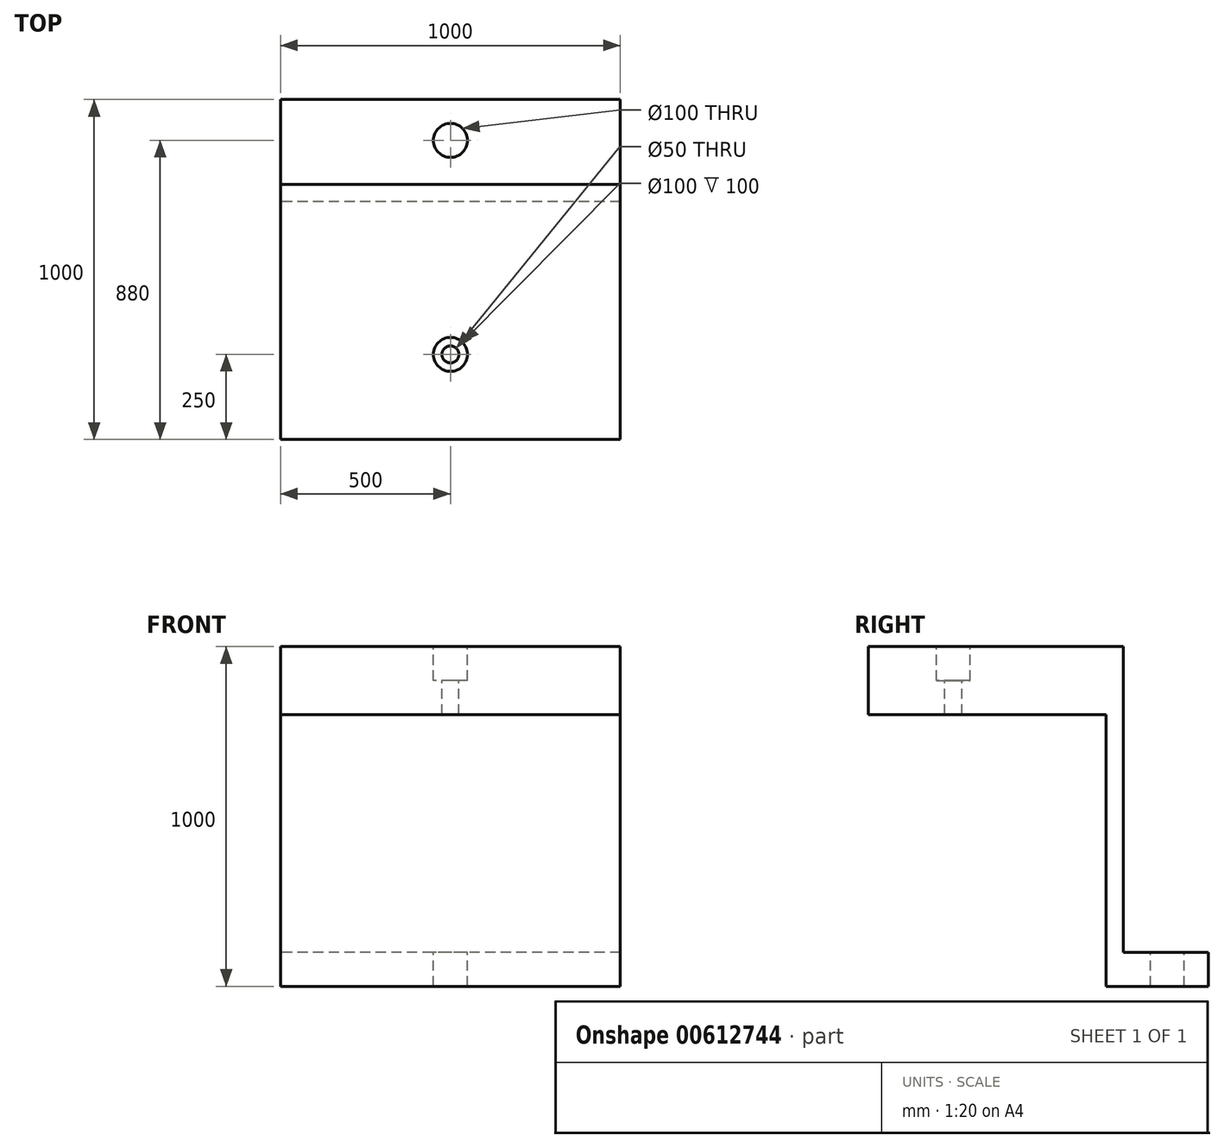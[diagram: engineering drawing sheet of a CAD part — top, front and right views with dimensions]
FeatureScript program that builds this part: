
annotation { "Feature Type Name" : "Feature", "Feature Type Description" : "" }
export const myFeature = defineFeature(function(context is Context, id is Id, definition is map)
    precondition{}
    {
        {
            var Q0;
            Q0=qCreatedBy(makeId("Right.planeOp"),FACE);
            var sketch = newSketch(context, id + "F0", { "sketchPlane" : qUnion([Q0])});
            skLineSegment(sketch, "E0", {"start": v(0, 0) * mm, "end": v(0, 100) * mm});
            skLineSegment(sketch, "E1", {"start": v(0, 100) * mm, "end": v(-250, 100) * mm});
            skLineSegment(sketch, "E2", {"start": v(-250, 100) * mm, "end": v(-250, 1000) * mm});
            skLineSegment(sketch, "E3", {"start": v(-250, 1000) * mm, "end": v(-1000, 1000) * mm});
            skLineSegment(sketch, "E4", {"start": v(-1000, 1000) * mm, "end": v(-1000, 800) * mm});
            skLineSegment(sketch, "E5", {"start": v(-1000, 800) * mm, "end": v(-300, 800) * mm});
            skLineSegment(sketch, "E6", {"start": v(-300, 800) * mm, "end": v(-300, 0) * mm});
            skLineSegment(sketch, "E7", {"start": v(0, 0) * mm, "end": v(-300, 0) * mm});
            skSolve(sketch);
        }
        {
            var Q0;
            Q0=makeQuery(id+"F0.imprint","IMPRINT",FACE,{"disambiguationData":[TD([[makeQuery(id+"F0.imprint","IMPRINT",EDGE,{"derivedFrom":sQuery(id+"F0.wireOp",EDGE,"E0")}),1.0]])]});
            extrude(context, id + "F1", {"entities" : qUnion([Q0]), "depth" : 1000 * mm, "offsetDistance" : 25 * mm});
        }
        {
            var Q0;
            Q0=makeQuery(id+"F1.opExtrude","SWEPT_FACE",FACE,{"disambiguationData":[OSD([sQuery(id+"F0.wireOp",EDGE,"E1")])]});
            var sketch = newSketch(context, id + "F2", { "sketchPlane" : qUnion([Q0])});
            skPoint(sketch, "E8", {"position": v(500, -120) * mm});
            skSolve(sketch);
        }
        {
            var Q0;
            Q0=sQuery(id+"F2.wireOp",VERTEX,"E8");
            var Q1;
            Q1=makeQuery(id+"F1.opExtrude","SWEPT_BODY",BODY,{"disambiguationData":[OSD([sQuery(id+"F0.wireOp",EDGE,"E0"),sQuery(id+"F0.wireOp",EDGE,"E1"),sQuery(id+"F0.wireOp",EDGE,"E2"),sQuery(id+"F0.wireOp",EDGE,"E3"),sQuery(id+"F0.wireOp",EDGE,"E4"),sQuery(id+"F0.wireOp",EDGE,"E5"),sQuery(id+"F0.wireOp",EDGE,"E6"),sQuery(id+"F0.wireOp",EDGE,"E7")])]});
            hole(context, id + "F3", {"style" : HoleStyle.SIMPLE, "endStyle" : HoleEndStyle.THROUGH, "holeDiameter" : 100 * mm, "majorDiameter" : 5 * mm, "isTappedThrough" : true, "tappedDepth" : 12 * mm, "tapClearance" : 3, "locations" : qUnion([Q0]), "scope" : qUnion([Q1])});
        }
        {
            var Q0;
            Q0=makeQuery(id+"F1.opExtrude","SWEPT_FACE",FACE,{"disambiguationData":[OSD([sQuery(id+"F0.wireOp",EDGE,"E3")])]});
            var sketch = newSketch(context, id + "F4", { "sketchPlane" : qUnion([Q0])});
            skPoint(sketch, "E9", {"position": v(500, -750) * mm});
            skSolve(sketch);
        }
        {
            var Q0;
            Q0=sQuery(id+"F4.wireOp",VERTEX,"E9");
            var Q1;
            Q1=makeQuery(id+"F1.opExtrude","SWEPT_BODY",BODY,{"disambiguationData":[OSD([sQuery(id+"F0.wireOp",EDGE,"E0"),sQuery(id+"F0.wireOp",EDGE,"E1"),sQuery(id+"F0.wireOp",EDGE,"E2"),sQuery(id+"F0.wireOp",EDGE,"E3"),sQuery(id+"F0.wireOp",EDGE,"E4"),sQuery(id+"F0.wireOp",EDGE,"E5"),sQuery(id+"F0.wireOp",EDGE,"E6"),sQuery(id+"F0.wireOp",EDGE,"E7")])]});
            hole(context, id + "F5", {"style" : HoleStyle.C_BORE, "endStyle" : HoleEndStyle.THROUGH, "holeDiameter" : 50 * mm, "cBoreDiameter" : 100 * mm, "cBoreDepth" : 100 * mm, "majorDiameter" : 5 * mm, "isTappedThrough" : true, "tappedDepth" : 12 * mm, "tapClearance" : 3, "locations" : qUnion([Q0]), "scope" : qUnion([Q1])});
        }
    });
